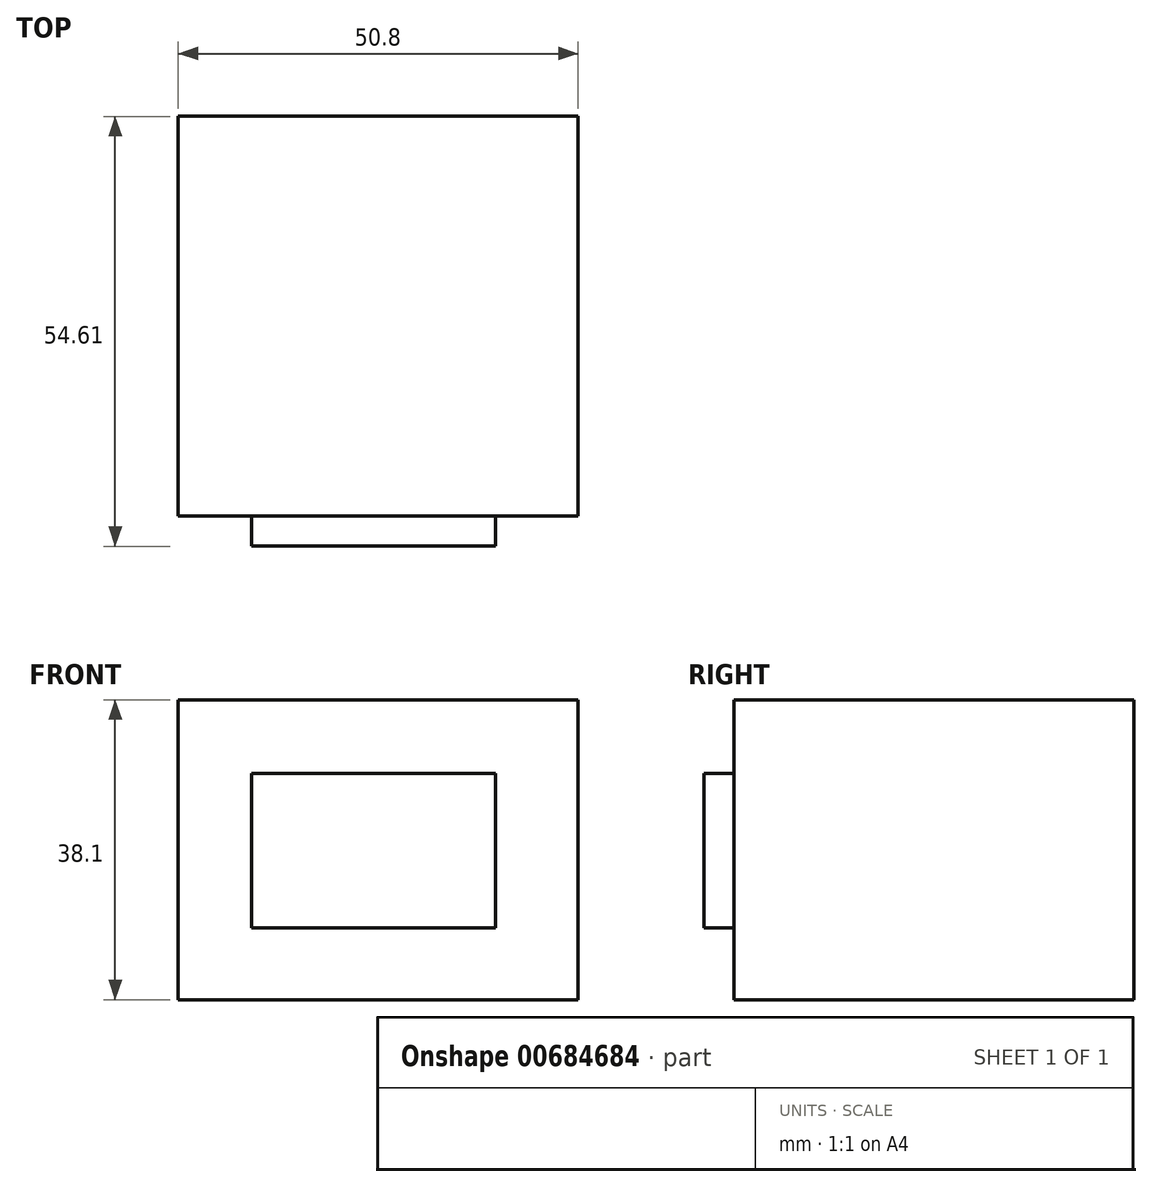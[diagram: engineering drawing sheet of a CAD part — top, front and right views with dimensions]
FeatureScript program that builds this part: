
annotation { "Feature Type Name" : "Feature", "Feature Type Description" : "" }
export const myFeature = defineFeature(function(context is Context, id is Id, definition is map)
    precondition{}
    {
        {
            var Q0;
            Q0=qCreatedBy(makeId("Top.planeOp"),FACE);
            var sketch = newSketch(context, id + "F0", { "sketchPlane" : qUnion([Q0])});
            skLineSegment(sketch, "E0.bottom", {"start": v(-23.1, 26.06) * mm, "end": v(27.7, 26.06) * mm});
            skLineSegment(sketch, "E0.top", {"start": v(-23.1, -24.74) * mm, "end": v(27.7, -24.74) * mm});
            skLineSegment(sketch, "E0.left", {"start": v(-23.1, 26.06) * mm, "end": v(-23.1, -24.74) * mm});
            skLineSegment(sketch, "E0.right", {"start": v(27.7, 26.06) * mm, "end": v(27.7, -24.74) * mm});
            skSolve(sketch);
        }
        {
            var Q0;
            Q0=qSketchRegion(id+"F0",true);
            extrude(context, id + "F1", {"entities" : qUnion([Q0]), "depth" : 38.1 * mm, "offsetDistance" : 25.4 * mm});
        }
        {
            var Q0;
            Q0=makeQuery(id+"F1.opExtrude","SWEPT_FACE",FACE,{"disambiguationData":[OSD([sQuery(id+"F0.wireOp",EDGE,"E0.top")])]});
            var sketch = newSketch(context, id + "F2", { "sketchPlane" : qUnion([Q0])});
            skLineSegment(sketch, "E1.bottom", {"start": v(-13.77, 28.72) * mm, "end": v(17.22, 28.72) * mm});
            skLineSegment(sketch, "E1.top", {"start": v(-13.77, 9.11) * mm, "end": v(17.22, 9.11) * mm});
            skLineSegment(sketch, "E1.left", {"start": v(-13.77, 28.72) * mm, "end": v(-13.77, 9.11) * mm});
            skLineSegment(sketch, "E1.right", {"start": v(17.22, 28.72) * mm, "end": v(17.22, 9.11) * mm});
            skSolve(sketch);
        }
        {
            var Q0;
            Q0=qSketchRegion(id+"F2",true);
            extrude(context, id + "F3", {"entities" : qUnion([Q0]), "operationType" : NewBodyOperationType.ADD, "depth" : 3.8 * mm, "offsetDistance" : 25.4 * mm});
        }
    });
